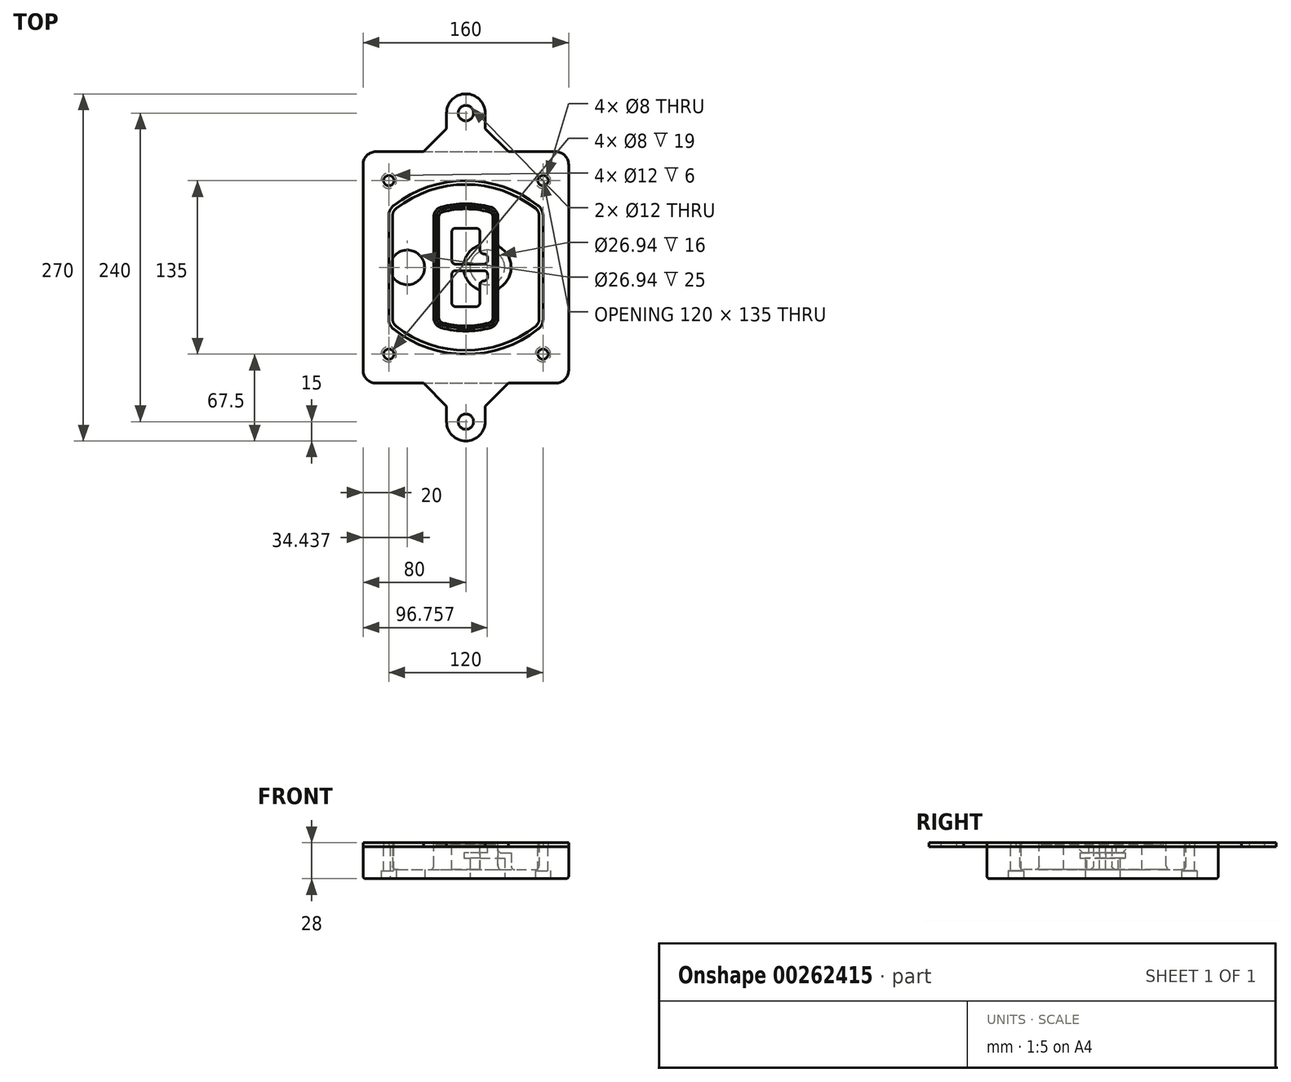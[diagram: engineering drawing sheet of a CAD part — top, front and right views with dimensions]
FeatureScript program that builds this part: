
annotation { "Feature Type Name" : "Feature", "Feature Type Description" : "" }
export const myFeature = defineFeature(function(context is Context, id is Id, definition is map)
    precondition{}
    {
        {
            var Q0;
            Q0=qCreatedBy(makeId("Top.planeOp"),FACE);
            var sketch = newSketch(context, id + "F0", { "sketchPlane" : qUnion([Q0])});
            skPoint(sketch, "E0.rect.middle", {"position": v(0, 0) * mm});
            skLineSegment(sketch, "E1.bottom", {"start": v(-70, -90) * mm, "end": v(70, -90) * mm});
            skLineSegment(sketch, "E1.top", {"start": v(-70, 90) * mm, "end": v(70, 90) * mm});
            skLineSegment(sketch, "E1.left", {"start": v(-80, -80) * mm, "end": v(-80, 80) * mm});
            skLineSegment(sketch, "E1.right", {"start": v(80, -80) * mm, "end": v(80, 80) * mm});
            skLineSegment(sketch, "E2", {"start": v(-80, 90) * mm, "end": v(80, -90) * mm, "construction": true});
            skLineSegment(sketch, "E3", {"start": v(80, 90) * mm, "end": v(-80, -90) * mm, "construction": true});
            skCircle(sketch, "E4", {"center": v(-60, 67.5) * mm, "radius": 4 * mm});
            skCircle(sketch, "E5", {"center": v(60, 67.5) * mm, "radius": 4 * mm});
            skCircle(sketch, "E6", {"center": v(60, -67.5) * mm, "radius": 4 * mm});
            skCircle(sketch, "E7", {"center": v(-60, -67.5) * mm, "radius": 4 * mm});
            skLineSegment(sketch, "E8", {"start": v(-60, 67.5) * mm, "end": v(60, 67.5) * mm, "construction": true});
            skLineSegment(sketch, "E9", {"start": v(60, 67.5) * mm, "end": v(60, -67.5) * mm, "construction": true});
            skLineSegment(sketch, "E10", {"start": v(60, -67.5) * mm, "end": v(-60, -67.5) * mm, "construction": true});
            skLineSegment(sketch, "E11", {"start": v(-60, -67.5) * mm, "end": v(-60, 67.5) * mm, "construction": true});
            skLineSegment(sketch, "E12", {"start": v(-60, 40.3) * mm, "end": v(-60, -40.3) * mm});
            skLineSegment(sketch, "E13", {"start": v(60, 40.3) * mm, "end": v(60, -40.3) * mm});
            skArc(sketch, "E14", {"start": v(56.15, 48.18) * mm, "mid": v(0, 67.5) * mm, "end": v(-56.15, 48.18) * mm});
            skArc(sketch, "E15", {"start": v(-56.15, -48.18) * mm, "mid": v(0, -67.5) * mm, "end": v(56.15, -48.18) * mm});
            skLineSegment(sketch, "E16", {"start": v(-60, 0) * mm, "end": v(60, 0) * mm, "construction": true});
            skPoint(sketch, "E17.visualSharp", {"position": v(-60, -45) * mm});
            skArc(sketch, "E17.filletArc", {"start": v(-60, -40.3) * mm, "mid": v(-58.99, -44.68) * mm, "end": v(-56.15, -48.18) * mm});
            skPoint(sketch, "E18.visualSharp", {"position": v(-60, 45) * mm});
            skArc(sketch, "E18.filletArc", {"start": v(-56.15, 48.18) * mm, "mid": v(-58.99, 44.68) * mm, "end": v(-60, 40.3) * mm});
            skPoint(sketch, "E19.visualSharp", {"position": v(60, 45) * mm});
            skArc(sketch, "E19.filletArc", {"start": v(60, 40.3) * mm, "mid": v(58.99, 44.68) * mm, "end": v(56.15, 48.18) * mm});
            skPoint(sketch, "E20.visualSharp", {"position": v(60, -45) * mm});
            skArc(sketch, "E20.filletArc", {"start": v(56.15, -48.18) * mm, "mid": v(58.99, -44.68) * mm, "end": v(60, -40.3) * mm});
            skPoint(sketch, "E21.visualSharp", {"position": v(-80, 90) * mm});
            skArc(sketch, "E21.filletArc", {"start": v(-70, 90) * mm, "mid": v(-77.07, 87.07) * mm, "end": v(-80, 80) * mm});
            skPoint(sketch, "E22.visualSharp", {"position": v(80, 90) * mm});
            skArc(sketch, "E22.filletArc", {"start": v(80, 80) * mm, "mid": v(77.07, 87.07) * mm, "end": v(70, 90) * mm});
            skPoint(sketch, "E23.visualSharp", {"position": v(80, -90) * mm});
            skArc(sketch, "E23.filletArc", {"start": v(70, -90) * mm, "mid": v(77.07, -87.07) * mm, "end": v(80, -80) * mm});
            skPoint(sketch, "E24.visualSharp", {"position": v(-80, -90) * mm});
            skArc(sketch, "E24.filletArc", {"start": v(-80, -80) * mm, "mid": v(-77.07, -87.07) * mm, "end": v(-70, -90) * mm});
            skArc(sketch, "E25.0", {"start": v(57, 40.3) * mm, "mid": v(56.3, 43.36) * mm, "end": v(54.3, 45.81) * mm});
            skLineSegment(sketch, "E25.1", {"start": v(57, 40.3) * mm, "end": v(57, -40.3) * mm});
            skArc(sketch, "E25.2", {"start": v(54.3, -45.81) * mm, "mid": v(56.3, -43.36) * mm, "end": v(57, -40.3) * mm});
            skArc(sketch, "E25.3", {"start": v(-54.3, -45.81) * mm, "mid": v(0, -64.5) * mm, "end": v(54.3, -45.81) * mm});
            skArc(sketch, "E25.4", {"start": v(-57, -40.3) * mm, "mid": v(-56.3, -43.36) * mm, "end": v(-54.3, -45.81) * mm});
            skArc(sketch, "E25.5", {"start": v(54.3, 45.81) * mm, "mid": v(0, 64.5) * mm, "end": v(-54.3, 45.81) * mm});
            skLineSegment(sketch, "E25.6", {"start": v(-57, 40.3) * mm, "end": v(-57, -40.3) * mm});
            skArc(sketch, "E25.7", {"start": v(-54.3, 45.81) * mm, "mid": v(-56.3, 43.36) * mm, "end": v(-57, 40.3) * mm});
            skArc(sketch, "E26.0", {"start": v(-58.62, 51.33) * mm, "mid": v(-62.58, 46.43) * mm, "end": v(-64, 40.3) * mm});
            skArc(sketch, "E26.1", {"start": v(58.62, 51.33) * mm, "mid": v(0, 71.5) * mm, "end": v(-58.62, 51.33) * mm});
            skArc(sketch, "E26.2", {"start": v(64, 40.3) * mm, "mid": v(62.58, 46.43) * mm, "end": v(58.62, 51.33) * mm});
            skLineSegment(sketch, "E26.3", {"start": v(64, 40.3) * mm, "end": v(64, -40.3) * mm});
            skArc(sketch, "E26.4", {"start": v(58.62, -51.33) * mm, "mid": v(62.58, -46.43) * mm, "end": v(64, -40.3) * mm});
            skLineSegment(sketch, "E26.5", {"start": v(-64, 40.3) * mm, "end": v(-64, -40.3) * mm});
            skArc(sketch, "E26.6", {"start": v(-58.62, -51.33) * mm, "mid": v(0, -71.5) * mm, "end": v(58.62, -51.33) * mm});
            skArc(sketch, "E26.7", {"start": v(-64, -40.3) * mm, "mid": v(-62.58, -46.43) * mm, "end": v(-58.62, -51.33) * mm});
            skSolve(sketch);
        }
        {
            var Q0;
            Q0=makeQuery(id+"F0.imprint","IMPRINT",FACE,{"disambiguationData":[TD([[makeQuery(id+"F0.imprint","IMPRINT",EDGE,{"derivedFrom":sQuery(id+"F0.wireOp",EDGE,"E1.bottom")}),1.0]])]});
            var Q1;
            Q1=makeQuery(id+"F0.imprint","IMPRINT",FACE,{"disambiguationData":[TD([[makeQuery(id+"F0.imprint","IMPRINT",EDGE,{"derivedFrom":sQuery(id+"F0.wireOp",EDGE,"E12")}),1.0]])]});
            var Q2;
            Q2=makeQuery(id+"F0.imprint","IMPRINT",FACE,{"disambiguationData":[TD([[makeQuery(id+"F0.imprint","IMPRINT",EDGE,{"derivedFrom":sQuery(id+"F0.wireOp",EDGE,"E25.0")}),1.0]])]});
            var Q3;
            Q3=makeQuery(id+"F0.imprint","IMPRINT",FACE,{"disambiguationData":[TD([[makeQuery(id+"F0.imprint","IMPRINT",EDGE,{"derivedFrom":sQuery(id+"F0.wireOp",EDGE,"E12")}),-1.0]])]});
            extrude(context, id + "F1", {"entities" : qUnion([Q0, Q1, Q2, Q3]), "oppositeDirection" : true, "depth" : 25 * mm});
        }
        {
            var Q0;
            Q0=makeQuery(id+"F0.imprint","IMPRINT",FACE,{"disambiguationData":[TD([[makeQuery(id+"F0.imprint","IMPRINT",EDGE,{"derivedFrom":sQuery(id+"F0.wireOp",EDGE,"E12")}),1.0]])]});
            extrude(context, id + "F2", {"entities" : qUnion([Q0]), "operationType" : NewBodyOperationType.ADD, "depth" : 3 * mm});
        }
        {
            var Q0;
            Q0=makeQuery(id+"F0.imprint","IMPRINT",FACE,{"disambiguationData":[TD([[makeQuery(id+"F0.imprint","IMPRINT",EDGE,{"derivedFrom":sQuery(id+"F0.wireOp",EDGE,"E25.0")}),1.0]])]});
            extrude(context, id + "F3", {"entities" : qUnion([Q0]), "operationType" : NewBodyOperationType.REMOVE, "oppositeDirection" : true, "depth" : 18 * mm});
        }
        {
            var Q0;
            Q0=makeQuery(id+"F2.opExtrude","CAP_FACE",FACE,{"disambiguationData":[OSD([sQuery(id+"F0.wireOp",EDGE,"E12"),sQuery(id+"F0.wireOp",EDGE,"E13"),sQuery(id+"F0.wireOp",EDGE,"E14"),sQuery(id+"F0.wireOp",EDGE,"E15"),sQuery(id+"F0.wireOp",EDGE,"E17.filletArc"),sQuery(id+"F0.wireOp",EDGE,"E18.filletArc"),sQuery(id+"F0.wireOp",EDGE,"E19.filletArc"),sQuery(id+"F0.wireOp",EDGE,"E20.filletArc"),sQuery(id+"F0.wireOp",EDGE,"E25.0"),sQuery(id+"F0.wireOp",EDGE,"E25.1"),sQuery(id+"F0.wireOp",EDGE,"E25.2"),sQuery(id+"F0.wireOp",EDGE,"E25.3"),sQuery(id+"F0.wireOp",EDGE,"E25.4"),sQuery(id+"F0.wireOp",EDGE,"E25.5"),sQuery(id+"F0.wireOp",EDGE,"E25.6"),sQuery(id+"F0.wireOp",EDGE,"E25.7")])],"isStart":false});
            var sketch = newSketch(context, id + "F4", { "sketchPlane" : qUnion([Q0])});
            skArc(sketch, "E27.0", {"start": v(-19.08, -46.97) * mm, "mid": v(0, -49.5) * mm, "end": v(19.08, -46.97) * mm});
            skArc(sketch, "E28.0", {"start": v(19.08, 46.97) * mm, "mid": v(0, 49.5) * mm, "end": v(-19.08, 46.97) * mm});
            skLineSegment(sketch, "E29", {"start": v(-25, 39.25) * mm, "end": v(-25, -39.25) * mm});
            skLineSegment(sketch, "E30", {"start": v(25, 39.25) * mm, "end": v(25, -39.25) * mm});
            skLineSegment(sketch, "E31", {"start": v(-25, 45.1) * mm, "end": v(25, 45.1) * mm, "construction": true});
            skLineSegment(sketch, "E32", {"start": v(-25, -45.1) * mm, "end": v(25, -45.1) * mm, "construction": true});
            skPoint(sketch, "E33.visualSharp", {"position": v(-25, 45.1) * mm});
            skArc(sketch, "E33.filletArc", {"start": v(-19.08, 46.97) * mm, "mid": v(-23.35, 44.11) * mm, "end": v(-25, 39.25) * mm});
            skPoint(sketch, "E34.visualSharp", {"position": v(25, 45.1) * mm});
            skArc(sketch, "E34.filletArc", {"start": v(25, 39.25) * mm, "mid": v(23.35, 44.11) * mm, "end": v(19.08, 46.97) * mm});
            skPoint(sketch, "E35.visualSharp", {"position": v(25, -45.1) * mm});
            skArc(sketch, "E35.filletArc", {"start": v(19.08, -46.97) * mm, "mid": v(23.35, -44.11) * mm, "end": v(25, -39.25) * mm});
            skPoint(sketch, "E36.visualSharp", {"position": v(-25, -45.1) * mm});
            skArc(sketch, "E36.filletArc", {"start": v(-25, -39.25) * mm, "mid": v(-23.35, -44.11) * mm, "end": v(-19.08, -46.97) * mm});
            skArc(sketch, "E37.0", {"start": v(54.3, 45.81) * mm, "mid": v(0, 64.5) * mm, "end": v(-54.3, 45.81) * mm});
            skArc(sketch, "E37.1", {"start": v(-54.3, 45.81) * mm, "mid": v(-56.3, 43.36) * mm, "end": v(-57, 40.3) * mm});
            skLineSegment(sketch, "E37.2", {"start": v(-57, 40.3) * mm, "end": v(-57, -40.3) * mm});
            skArc(sketch, "E37.3", {"start": v(-57, -40.3) * mm, "mid": v(-56.3, -43.36) * mm, "end": v(-54.3, -45.81) * mm});
            skArc(sketch, "E37.4", {"start": v(-54.3, -45.81) * mm, "mid": v(0, -64.5) * mm, "end": v(54.3, -45.81) * mm});
            skArc(sketch, "E37.5", {"start": v(54.3, -45.81) * mm, "mid": v(56.3, -43.36) * mm, "end": v(57, -40.3) * mm});
            skLineSegment(sketch, "E37.6", {"start": v(57, 40.3) * mm, "end": v(57, -40.3) * mm});
            skArc(sketch, "E37.7", {"start": v(57, 40.3) * mm, "mid": v(56.3, 43.36) * mm, "end": v(54.3, 45.81) * mm});
            skLineSegment(sketch, "E38.0", {"start": v(23, 39.25) * mm, "end": v(23, -39.25) * mm});
            skArc(sketch, "E38.1", {"start": v(18.56, -45.04) * mm, "mid": v(21.76, -42.9) * mm, "end": v(23, -39.25) * mm});
            skArc(sketch, "E38.2", {"start": v(-18.56, -45.04) * mm, "mid": v(0, -47.5) * mm, "end": v(18.56, -45.04) * mm});
            skArc(sketch, "E38.3", {"start": v(-23, -39.25) * mm, "mid": v(-21.76, -42.9) * mm, "end": v(-18.56, -45.04) * mm});
            skLineSegment(sketch, "E38.4", {"start": v(-23, 39.25) * mm, "end": v(-23, -39.25) * mm});
            skArc(sketch, "E38.5", {"start": v(23, 39.25) * mm, "mid": v(21.76, 42.9) * mm, "end": v(18.56, 45.04) * mm});
            skArc(sketch, "E38.6", {"start": v(-18.56, 45.04) * mm, "mid": v(-21.76, 42.9) * mm, "end": v(-23, 39.25) * mm});
            skArc(sketch, "E38.7", {"start": v(18.56, 45.04) * mm, "mid": v(0, 47.5) * mm, "end": v(-18.56, 45.04) * mm});
            skArc(sketch, "E39.0", {"start": v(21, 39.25) * mm, "mid": v(20.18, 41.68) * mm, "end": v(18.04, 43.1) * mm});
            skLineSegment(sketch, "E39.1", {"start": v(21, 39.25) * mm, "end": v(21, -39.25) * mm});
            skArc(sketch, "E39.2", {"start": v(18.04, -43.1) * mm, "mid": v(20.18, -41.68) * mm, "end": v(21, -39.25) * mm});
            skArc(sketch, "E39.3", {"start": v(-18.04, -43.1) * mm, "mid": v(0, -45.5) * mm, "end": v(18.04, -43.1) * mm});
            skArc(sketch, "E39.4", {"start": v(-21, -39.25) * mm, "mid": v(-20.18, -41.68) * mm, "end": v(-18.04, -43.1) * mm});
            skArc(sketch, "E39.5", {"start": v(18.04, 43.1) * mm, "mid": v(0, 45.5) * mm, "end": v(-18.04, 43.1) * mm});
            skLineSegment(sketch, "E39.6", {"start": v(-21, 39.25) * mm, "end": v(-21, -39.25) * mm});
            skArc(sketch, "E39.7", {"start": v(-18.04, 43.1) * mm, "mid": v(-20.18, 41.68) * mm, "end": v(-21, 39.25) * mm});
            skLineSegment(sketch, "E40", {"start": v(-25, 0) * mm, "end": v(25, 0) * mm, "construction": true});
            skLineSegment(sketch, "E41", {"start": v(-11, 5.5) * mm, "end": v(-11, 27.5) * mm});
            skLineSegment(sketch, "E42", {"start": v(-8, 30.5) * mm, "end": v(8, 30.5) * mm});
            skLineSegment(sketch, "E43", {"start": v(11, 27.5) * mm, "end": v(11, 13.5) * mm});
            skLineSegment(sketch, "E44", {"start": v(14, 10.5) * mm, "end": v(14, 10.5) * mm});
            skLineSegment(sketch, "E45", {"start": v(17, 7.5) * mm, "end": v(17, 5.5) * mm});
            skLineSegment(sketch, "E46", {"start": v(14, 2.5) * mm, "end": v(-8, 2.5) * mm});
            skPoint(sketch, "E47.visualSharp", {"position": v(-11, 30.5) * mm});
            skArc(sketch, "E47.filletArc", {"start": v(-8, 30.5) * mm, "mid": v(-10.12, 29.62) * mm, "end": v(-11, 27.5) * mm});
            skPoint(sketch, "E48.visualSharp", {"position": v(11, 30.5) * mm});
            skArc(sketch, "E48.filletArc", {"start": v(11, 27.5) * mm, "mid": v(10.12, 29.62) * mm, "end": v(8, 30.5) * mm});
            skPoint(sketch, "E49.visualSharp", {"position": v(11, 10.5) * mm});
            skArc(sketch, "E49.filletArc", {"start": v(11, 13.5) * mm, "mid": v(11.88, 11.38) * mm, "end": v(14, 10.5) * mm});
            skPoint(sketch, "E50.visualSharp", {"position": v(17, 10.5) * mm});
            skArc(sketch, "E50.filletArc", {"start": v(17, 7.5) * mm, "mid": v(16.12, 9.62) * mm, "end": v(14, 10.5) * mm});
            skPoint(sketch, "E51.visualSharp", {"position": v(17, 2.5) * mm});
            skArc(sketch, "E51.filletArc", {"start": v(14, 2.5) * mm, "mid": v(16.12, 3.38) * mm, "end": v(17, 5.5) * mm});
            skPoint(sketch, "E52.visualSharp", {"position": v(-11, 2.5) * mm});
            skArc(sketch, "E52.filletArc", {"start": v(-11, 5.5) * mm, "mid": v(-10.12, 3.38) * mm, "end": v(-8, 2.5) * mm});
            skLineSegment(sketch, "E53.0.MirrorCS", {"start": v(14, -2.5) * mm, "end": v(-8, -2.5) * mm});
            skArc(sketch, "E54.0.MirrorCS", {"start": v(-11, -5.5) * mm, "mid": v(-10.12, -3.38) * mm, "end": v(-8, -2.5) * mm});
            skLineSegment(sketch, "E55.0.MirrorCS", {"start": v(-11, -5.5) * mm, "end": v(-11, -27.5) * mm});
            skArc(sketch, "E56.0.MirrorCS", {"start": v(-8, -30.5) * mm, "mid": v(-10.12, -29.62) * mm, "end": v(-11, -27.5) * mm});
            skLineSegment(sketch, "E57.0.MirrorCS", {"start": v(-8, -30.5) * mm, "end": v(8, -30.5) * mm});
            skArc(sketch, "E58.0.MirrorCS", {"start": v(11, -27.5) * mm, "mid": v(10.12, -29.62) * mm, "end": v(8, -30.5) * mm});
            skLineSegment(sketch, "E59.0.MirrorCS", {"start": v(11, -27.5) * mm, "end": v(11, -13.5) * mm});
            skArc(sketch, "E60.0.MirrorCS", {"start": v(11, -13.5) * mm, "mid": v(11.88, -11.38) * mm, "end": v(14, -10.5) * mm});
            skArc(sketch, "E61.0.MirrorCS", {"start": v(17, -7.5) * mm, "mid": v(16.12, -9.62) * mm, "end": v(14, -10.5) * mm});
            skLineSegment(sketch, "E62.0.MirrorCS", {"start": v(17, -7.5) * mm, "end": v(17, -5.5) * mm});
            skArc(sketch, "E63.0.MirrorCS", {"start": v(14, -2.5) * mm, "mid": v(16.12, -3.38) * mm, "end": v(17, -5.5) * mm});
            skSolve(sketch);
        }
        {
            var Q0;
            Q0=makeQuery(id+"F4.imprint","IMPRINT",FACE,{"disambiguationData":[TD([[makeQuery(id+"F4.imprint","IMPRINT",EDGE,{"derivedFrom":sQuery(id+"F4.wireOp",EDGE,"E27.0")}),1.0]])]});
            var Q1;
            Q1=makeQuery(id+"F4.imprint","IMPRINT",FACE,{"disambiguationData":[TD([[makeQuery(id+"F4.imprint","IMPRINT",EDGE,{"derivedFrom":sQuery(id+"F4.wireOp",EDGE,"E38.0")}),-1.0]])]});
            var Q2;
            Q2=makeQuery(id+"F4.imprint","IMPRINT",FACE,{"disambiguationData":[TD([[makeQuery(id+"F4.imprint","IMPRINT",EDGE,{"derivedFrom":sQuery(id+"F4.wireOp",EDGE,"E39.0")}),1.0]])]});
            extrude(context, id + "F5", {"entities" : qUnion([Q0, Q1, Q2]), "operationType" : NewBodyOperationType.ADD, "endBound" : BoundingType.UP_TO_NEXT, "oppositeDirection" : true, "depth" : 25 * mm});
        }
        {
            var Q0;
            Q0=makeQuery(id+"F4.imprint","IMPRINT",FACE,{"disambiguationData":[TD([[makeQuery(id+"F4.imprint","IMPRINT",EDGE,{"derivedFrom":sQuery(id+"F4.wireOp",EDGE,"E38.0")}),-1.0]])]});
            extrude(context, id + "F6", {"entities" : qUnion([Q0]), "operationType" : NewBodyOperationType.REMOVE, "oppositeDirection" : true, "depth" : 2 * mm});
        }
        {
            var Q0;
            Q0=makeQuery(id+"F1.opExtrude","CAP_FACE",FACE,{"disambiguationData":[OSD([sQuery(id+"F0.wireOp",EDGE,"E1.bottom"),sQuery(id+"F0.wireOp",EDGE,"E1.top"),sQuery(id+"F0.wireOp",EDGE,"E1.left"),sQuery(id+"F0.wireOp",EDGE,"E1.right"),sQuery(id+"F0.wireOp",EDGE,"E4"),sQuery(id+"F0.wireOp",EDGE,"E5"),sQuery(id+"F0.wireOp",EDGE,"E6"),sQuery(id+"F0.wireOp",EDGE,"E7"),sQuery(id+"F0.wireOp",EDGE,"E21.filletArc"),sQuery(id+"F0.wireOp",EDGE,"E22.filletArc"),sQuery(id+"F0.wireOp",EDGE,"E23.filletArc"),sQuery(id+"F0.wireOp",EDGE,"E24.filletArc")])],"isStart":false});
            var sketch = newSketch(context, id + "F7", { "sketchPlane" : qUnion([Q0])});
            skCircle(sketch, "E64", {"center": v(16.76, 0) * mm, "radius": 13.47 * mm});
            skCircle(sketch, "E65", {"center": v(-45.56, 0) * mm, "radius": 13.47 * mm});
            skLineSegment(sketch, "E66", {"start": v(80, 0) * mm, "end": v(-80, 0) * mm});
            skCircle(sketch, "E67", {"center": v(16.76, 0) * mm, "radius": 18.47 * mm});
            skCircle(sketch, "E68", {"center": v(60, -67.5) * mm, "radius": 6 * mm});
            skCircle(sketch, "E69", {"center": v(-60, -67.5) * mm, "radius": 6 * mm});
            skCircle(sketch, "E70", {"center": v(-60, 67.5) * mm, "radius": 6 * mm});
            skCircle(sketch, "E71", {"center": v(60, 67.5) * mm, "radius": 6 * mm});
            skSolve(sketch);
        }
        {
            var Q0;
            {var subQ1=sQuery(id+"F7.wireOp",EDGE,"E66");var subQ4=sQuery(id+"F7.wireOp",EDGE,"E64");var subQ6=makeQuery(id+"F7.imprint","INTERSECT",VERTEX,{"disambiguationData":[OD(0.0)],"derivedFrom":[subQ4,subQ1]});Q0=makeQuery(id+"F7.imprint","IMPRINT",FACE,{"disambiguationData":[TD([[makeQuery(id+"F7.imprint","IMPRINT",EDGE,{"disambiguationData":[TD([[subQ6,-1.0]])],"derivedFrom":subQ4}),-1.0]])]});}
            var Q1;
            {var subQ0=sQuery(id+"F7.wireOp",EDGE,"E66");var subQ1=sQuery(id+"F7.wireOp",EDGE,"E64");var subQ3=makeQuery(id+"F7.imprint","INTERSECT",VERTEX,{"disambiguationData":[OD(0.0)],"derivedFrom":[subQ1,subQ0]});Q1=makeQuery(id+"F7.imprint","IMPRINT",FACE,{"disambiguationData":[TD([[makeQuery(id+"F7.imprint","IMPRINT",EDGE,{"disambiguationData":[TD([[subQ3,-1.0]])],"derivedFrom":subQ1}),1.0]])]});}
            var Q2;
            {var subQ0=sQuery(id+"F7.wireOp",EDGE,"E66");var subQ1=sQuery(id+"F7.wireOp",EDGE,"E64");var subQ3=makeQuery(id+"F7.imprint","INTERSECT",VERTEX,{"disambiguationData":[OD(0.0)],"derivedFrom":[subQ1,subQ0]});Q2=makeQuery(id+"F7.imprint","IMPRINT",FACE,{"disambiguationData":[TD([[makeQuery(id+"F7.imprint","IMPRINT",EDGE,{"disambiguationData":[TD([[subQ3,1.0]])],"derivedFrom":subQ1}),1.0]])]});}
            var Q3;
            {var subQ1=sQuery(id+"F7.wireOp",EDGE,"E66");var subQ4=sQuery(id+"F7.wireOp",EDGE,"E64");var subQ6=makeQuery(id+"F7.imprint","INTERSECT",VERTEX,{"disambiguationData":[OD(0.0)],"derivedFrom":[subQ4,subQ1]});Q3=makeQuery(id+"F7.imprint","IMPRINT",FACE,{"disambiguationData":[TD([[makeQuery(id+"F7.imprint","IMPRINT",EDGE,{"disambiguationData":[TD([[subQ6,1.0]])],"derivedFrom":subQ4}),-1.0]])]});}
            extrude(context, id + "F8", {"entities" : qUnion([Q0, Q1, Q2, Q3]), "operationType" : NewBodyOperationType.ADD, "oppositeDirection" : true, "depth" : 20 * mm});
        }
        {
            var Q0;
            {var subQ0=sQuery(id+"F7.wireOp",EDGE,"E66");var subQ1=sQuery(id+"F7.wireOp",EDGE,"E64");var subQ3=makeQuery(id+"F7.imprint","INTERSECT",VERTEX,{"disambiguationData":[OD(0.0)],"derivedFrom":[subQ1,subQ0]});Q0=makeQuery(id+"F7.imprint","IMPRINT",FACE,{"disambiguationData":[TD([[makeQuery(id+"F7.imprint","IMPRINT",EDGE,{"disambiguationData":[TD([[subQ3,-1.0]])],"derivedFrom":subQ1}),1.0]])]});}
            var Q1;
            {var subQ0=sQuery(id+"F7.wireOp",EDGE,"E66");var subQ1=sQuery(id+"F7.wireOp",EDGE,"E64");var subQ3=makeQuery(id+"F7.imprint","INTERSECT",VERTEX,{"disambiguationData":[OD(0.0)],"derivedFrom":[subQ1,subQ0]});Q1=makeQuery(id+"F7.imprint","IMPRINT",FACE,{"disambiguationData":[TD([[makeQuery(id+"F7.imprint","IMPRINT",EDGE,{"disambiguationData":[TD([[subQ3,1.0]])],"derivedFrom":subQ1}),1.0]])]});}
            extrude(context, id + "F9", {"entities" : qUnion([Q0, Q1]), "operationType" : NewBodyOperationType.REMOVE, "oppositeDirection" : true, "depth" : 16 * mm});
        }
        {
            var Q0;
            {var subQ0=sQuery(id+"F7.wireOp",EDGE,"E66");var subQ1=sQuery(id+"F7.wireOp",EDGE,"E65");var subQ3=makeQuery(id+"F7.imprint","INTERSECT",VERTEX,{"disambiguationData":[OD(0.0)],"derivedFrom":[subQ1,subQ0]});Q0=makeQuery(id+"F7.imprint","IMPRINT",FACE,{"disambiguationData":[TD([[makeQuery(id+"F7.imprint","IMPRINT",EDGE,{"disambiguationData":[TD([[subQ3,-1.0]])],"derivedFrom":subQ1}),1.0]])]});}
            var Q1;
            {var subQ0=sQuery(id+"F7.wireOp",EDGE,"E66");var subQ1=sQuery(id+"F7.wireOp",EDGE,"E65");var subQ3=makeQuery(id+"F7.imprint","INTERSECT",VERTEX,{"disambiguationData":[OD(0.0)],"derivedFrom":[subQ1,subQ0]});Q1=makeQuery(id+"F7.imprint","IMPRINT",FACE,{"disambiguationData":[TD([[makeQuery(id+"F7.imprint","IMPRINT",EDGE,{"disambiguationData":[TD([[subQ3,1.0]])],"derivedFrom":subQ1}),1.0]])]});}
            extrude(context, id + "F10", {"entities" : qUnion([Q0, Q1]), "operationType" : NewBodyOperationType.REMOVE, "oppositeDirection" : true, "depth" : 25 * mm});
        }
        {
            var Q0;
            Q0=makeQuery(id+"F7.imprint","IMPRINT",FACE,{"disambiguationData":[TD([[makeQuery(id+"F7.imprint","IMPRINT",EDGE,{"derivedFrom":sQuery(id+"F7.wireOp",EDGE,"E68")}),1.0]])]});
            var Q1;
            Q1=makeQuery(id+"F7.imprint","IMPRINT",FACE,{"disambiguationData":[TD([[makeQuery(id+"F7.imprint","IMPRINT",EDGE,{"derivedFrom":makeQuery(id+"F1.opExtrude","CAP_EDGE",EDGE,{"disambiguationData":[OSD([sQuery(id+"F0.wireOp",EDGE,"E5")])],"isStart":false})}),-1.0]])]});
            var Q2;
            Q2=makeQuery(id+"F7.imprint","IMPRINT",FACE,{"disambiguationData":[TD([[makeQuery(id+"F7.imprint","IMPRINT",EDGE,{"derivedFrom":sQuery(id+"F7.wireOp",EDGE,"E69")}),1.0]])]});
            var Q3;
            Q3=makeQuery(id+"F7.imprint","IMPRINT",FACE,{"disambiguationData":[TD([[makeQuery(id+"F7.imprint","IMPRINT",EDGE,{"derivedFrom":makeQuery(id+"F1.opExtrude","CAP_EDGE",EDGE,{"disambiguationData":[OSD([sQuery(id+"F0.wireOp",EDGE,"E4")])],"isStart":false})}),-1.0]])]});
            var Q4;
            Q4=makeQuery(id+"F7.imprint","IMPRINT",FACE,{"disambiguationData":[TD([[makeQuery(id+"F7.imprint","IMPRINT",EDGE,{"derivedFrom":sQuery(id+"F7.wireOp",EDGE,"E70")}),1.0]])]});
            var Q5;
            Q5=makeQuery(id+"F7.imprint","IMPRINT",FACE,{"disambiguationData":[TD([[makeQuery(id+"F7.imprint","IMPRINT",EDGE,{"derivedFrom":makeQuery(id+"F1.opExtrude","CAP_EDGE",EDGE,{"disambiguationData":[OSD([sQuery(id+"F0.wireOp",EDGE,"E7")])],"isStart":false})}),-1.0]])]});
            var Q6;
            Q6=makeQuery(id+"F7.imprint","IMPRINT",FACE,{"disambiguationData":[TD([[makeQuery(id+"F7.imprint","IMPRINT",EDGE,{"derivedFrom":sQuery(id+"F7.wireOp",EDGE,"E71")}),1.0]])]});
            var Q7;
            Q7=makeQuery(id+"F7.imprint","IMPRINT",FACE,{"disambiguationData":[TD([[makeQuery(id+"F7.imprint","IMPRINT",EDGE,{"derivedFrom":makeQuery(id+"F1.opExtrude","CAP_EDGE",EDGE,{"disambiguationData":[OSD([sQuery(id+"F0.wireOp",EDGE,"E6")])],"isStart":false})}),-1.0]])]});
            extrude(context, id + "F11", {"entities" : qUnion([Q0, Q1, Q2, Q3, Q4, Q5, Q6, Q7]), "operationType" : NewBodyOperationType.REMOVE, "oppositeDirection" : true, "depth" : 6 * mm});
        }
        {
            var Q0;
            Q0=makeQuery(id+"F9.boolean.opBoolean","COPY",FACE,{"derivedFrom":makeQuery(id+"F9.opExtrude","CAP_FACE",FACE,{"disambiguationData":[OSD([sQuery(id+"F7.wireOp",EDGE,"E64")])],"isStart":false})});
            var sketch = newSketch(context, id + "F12", { "sketchPlane" : qUnion([Q0])});
            skArc(sketch, "E72.0", {"start": v(11, 17.55) * mm, "mid": v(2.57, 11.82) * mm, "end": v(-1.54, 2.5) * mm});
            skArc(sketch, "E72.1", {"start": v(-1.54, -2.5) * mm, "mid": v(2.57, -11.82) * mm, "end": v(11, -17.55) * mm});
            skLineSegment(sketch, "E73", {"start": v(-1.54, -2.5) * mm, "end": v(14, -2.5) * mm});
            skLineSegment(sketch, "E74.0", {"start": v(14, 2.5) * mm, "end": v(-1.54, 2.5) * mm});
            skArc(sketch, "E74.1", {"start": v(14, 2.5) * mm, "mid": v(16.12, 3.38) * mm, "end": v(17, 5.5) * mm});
            skLineSegment(sketch, "E74.2", {"start": v(17, 7.5) * mm, "end": v(17, 5.5) * mm});
            skArc(sketch, "E74.3", {"start": v(17, 7.5) * mm, "mid": v(16.12, 9.62) * mm, "end": v(14, 10.5) * mm});
            skArc(sketch, "E74.4", {"start": v(11, 13.5) * mm, "mid": v(11.88, 11.38) * mm, "end": v(14, 10.5) * mm});
            skLineSegment(sketch, "E74.5", {"start": v(11, 17.55) * mm, "end": v(11, 13.5) * mm});
            skLineSegment(sketch, "E74.7", {"start": v(14, -2.5) * mm, "end": v(-1.54, -2.5) * mm});
            skArc(sketch, "E74.8", {"start": v(14, -2.5) * mm, "mid": v(16.12, -3.38) * mm, "end": v(17, -5.5) * mm});
            skLineSegment(sketch, "E74.9", {"start": v(17, -7.5) * mm, "end": v(17, -5.5) * mm});
            skArc(sketch, "E74.10", {"start": v(17, -7.5) * mm, "mid": v(16.12, -9.62) * mm, "end": v(14, -10.5) * mm});
            skArc(sketch, "E74.11", {"start": v(11, -13.5) * mm, "mid": v(11.88, -11.38) * mm, "end": v(14, -10.5) * mm});
            skLineSegment(sketch, "E74.12", {"start": v(11, -17.55) * mm, "end": v(11, -13.5) * mm});
            skPoint(sketch, "E75.orphan", {"position": v(11, -27.5) * mm});
            skPoint(sketch, "E76.orphan", {"position": v(-8, -2.5) * mm});
            skPoint(sketch, "E77.orphan", {"position": v(-8, 2.5) * mm});
            skPoint(sketch, "E78.orphan", {"position": v(11, 27.5) * mm});
            skSolve(sketch);
        }
        {
            var Q0;
            {var subQ7=sQuery(id+"F12.wireOp",EDGE,"E72.0");var subQ14=sQuery(id+"F12.wireOp",EDGE,"E72.1");var subQ16=sQuery(id+"F12.wireOp",EDGE,"E74.1");var subQ18=sQuery(id+"F12.wireOp",EDGE,"E74.8");Q0=qUnion([makeQuery(id+"F12.imprint","IMPRINT",FACE,{"disambiguationData":[TD([[makeQuery(id+"F12.imprint","IMPRINT",EDGE,{"derivedFrom":subQ7}),1.0]])]}),makeQuery(id+"F12.imprint","IMPRINT",FACE,{"disambiguationData":[TD([[makeQuery(id+"F12.imprint","IMPRINT",EDGE,{"derivedFrom":subQ14}),1.0]])]}),makeQuery(id+"F12.imprint","IMPRINT",FACE,{"disambiguationData":[TD([[makeQuery(id+"F12.imprint","IMPRINT",EDGE,{"derivedFrom":subQ16}),1.0]])]}),makeQuery(id+"F12.imprint","IMPRINT",FACE,{"disambiguationData":[TD([[makeQuery(id+"F12.imprint","IMPRINT",EDGE,{"derivedFrom":subQ18}),-1.0]])]})]);}
            var Q1;
            Q1=makeQuery(id+"F5.boolean.opBoolean","SPLIT",FACE,{"disambiguationData":[TD([makeQuery(id+"F5.opExtrude","SWEPT_FACE",FACE,{"disambiguationData":[OSD([sQuery(id+"F4.wireOp",EDGE,"E41")])]})])],"derivedFrom":makeQuery(id+"F3.boolean.opBoolean","COPY",FACE,{"derivedFrom":makeQuery(id+"F3.opExtrude","CAP_FACE",FACE,{"disambiguationData":[OSD([sQuery(id+"F0.wireOp",EDGE,"E25.0"),sQuery(id+"F0.wireOp",EDGE,"E25.1"),sQuery(id+"F0.wireOp",EDGE,"E25.2"),sQuery(id+"F0.wireOp",EDGE,"E25.3"),sQuery(id+"F0.wireOp",EDGE,"E25.4"),sQuery(id+"F0.wireOp",EDGE,"E25.5"),sQuery(id+"F0.wireOp",EDGE,"E25.6"),sQuery(id+"F0.wireOp",EDGE,"E25.7")])],"isStart":false})})});
            extrude(context, id + "F13", {"entities" : qUnion([Q0]), "operationType" : NewBodyOperationType.REMOVE, "endBound" : BoundingType.UP_TO_SURFACE, "endBoundEntityFace" : qUnion([Q1]), "depth" : 25 * mm});
        }
        {
            var Q0;
            Q0=makeQuery(id+"F3.boolean.opBoolean","COPY",EDGE,{"derivedFrom":makeQuery(id+"F3.opExtrude","CAP_EDGE",EDGE,{"disambiguationData":[OSD([sQuery(id+"F0.wireOp",EDGE,"E25.6")])],"isStart":false})});
            var Q1;
            Q1=makeQuery(id+"F8.boolean.opBoolean","INTERSECT",EDGE,{"derivedFrom":[makeQuery(id+"F5.opExtrude","SWEPT_FACE",FACE,{"disambiguationData":[OSD([sQuery(id+"F4.wireOp",EDGE,"E30")])]}),makeQuery(id+"F8.opExtrude","CAP_FACE",FACE,{"disambiguationData":[OSD([sQuery(id+"F7.wireOp",EDGE,"E67")])],"isStart":false})]});
            var Q2;
            Q2=makeQuery(id+"F8.boolean.opBoolean","INTERSECT",EDGE,{"disambiguationData":[OD(1.0)],"derivedFrom":[makeQuery(id+"F5.opExtrude","SWEPT_FACE",FACE,{"disambiguationData":[OSD([sQuery(id+"F4.wireOp",EDGE,"E30")])]}),makeQuery(id+"F8.opExtrude","SWEPT_FACE",FACE,{"disambiguationData":[OSD([sQuery(id+"F7.wireOp",EDGE,"E67")])]})]});
            var Q3;
            {var subQ0=sQuery(id+"F4.wireOp",EDGE,"E30");Q3=makeQuery(id+"F8.boolean.opBoolean","SPLIT",EDGE,{"disambiguationData":[TD([makeQuery(id+"F5.opExtrude","SWEPT_FACE",FACE,{"disambiguationData":[OSD([sQuery(id+"F4.wireOp",EDGE,"E35.filletArc")])]})])],"derivedFrom":makeQuery(id+"F5.opExtrude","CAP_EDGE",EDGE,{"disambiguationData":[OSD([subQ0])],"isStart":false})});}
            var Q4;
            {var subQ0=sQuery(id+"F0.wireOp",EDGE,"E25.7");var subQ1=sQuery(id+"F0.wireOp",EDGE,"E25.1");var subQ2=sQuery(id+"F0.wireOp",EDGE,"E25.6");var subQ3=sQuery(id+"F0.wireOp",EDGE,"E25.5");var subQ4=sQuery(id+"F0.wireOp",EDGE,"E25.4");var subQ5=sQuery(id+"F0.wireOp",EDGE,"E25.0");var subQ6=sQuery(id+"F0.wireOp",EDGE,"E25.2");var subQ7=sQuery(id+"F0.wireOp",EDGE,"E25.3");Q4=makeQuery(id+"F8.boolean.opBoolean","INTERSECT",EDGE,{"derivedFrom":[makeQuery(id+"F5.boolean.opBoolean","SPLIT",FACE,{"disambiguationData":[TD([makeQuery(id+"F2.opExtrude","SWEPT_FACE",FACE,{"disambiguationData":[OSD([subQ5])]})])],"derivedFrom":makeQuery(id+"F3.boolean.opBoolean","COPY",FACE,{"derivedFrom":makeQuery(id+"F3.opExtrude","CAP_FACE",FACE,{"disambiguationData":[OSD([subQ5,subQ1,subQ6,subQ7,subQ4,subQ3,subQ2,subQ0])],"isStart":false})})}),makeQuery(id+"F8.opExtrude","SWEPT_FACE",FACE,{"disambiguationData":[OSD([sQuery(id+"F7.wireOp",EDGE,"E67")])]})]});}
            var Q5;
            Q5=makeQuery(id+"F8.boolean.opBoolean","INTERSECT",EDGE,{"disambiguationData":[OD(0.0)],"derivedFrom":[makeQuery(id+"F5.opExtrude","SWEPT_FACE",FACE,{"disambiguationData":[OSD([sQuery(id+"F4.wireOp",EDGE,"E30")])]}),makeQuery(id+"F8.opExtrude","SWEPT_FACE",FACE,{"disambiguationData":[OSD([sQuery(id+"F7.wireOp",EDGE,"E67")])]})]});
            fillet(context, id + "F14", {"entities" : qUnion([Q0, Q1, Q2, Q3, Q4, Q5]), "radius" : 3 * mm, "tangentPropagation" : true, "allowEdgeOverflow" : false});
        }
        {
            var Q0;
            Q0=makeQuery(id+"F1.opExtrude","CAP_EDGE",EDGE,{"disambiguationData":[OSD([sQuery(id+"F0.wireOp",EDGE,"E1.bottom")])],"isStart":false});
            fillet(context, id + "F15", {"entities" : qUnion([Q0]), "radius" : 2 * mm, "tangentPropagation" : true, "allowEdgeOverflow" : false});
        }
        {
            var Q0;
            {var subQ0=sQuery(id+"F0.wireOp",EDGE,"E22.filletArc");var subQ1=sQuery(id+"F0.wireOp",EDGE,"E7");var subQ2=sQuery(id+"F0.wireOp",EDGE,"E6");var subQ3=sQuery(id+"F0.wireOp",EDGE,"E5");var subQ4=sQuery(id+"F0.wireOp",EDGE,"E4");var subQ5=sQuery(id+"F0.wireOp",EDGE,"E1.bottom");var subQ6=sQuery(id+"F0.wireOp",EDGE,"E21.filletArc");var subQ7=sQuery(id+"F0.wireOp",EDGE,"E1.top");var subQ8=sQuery(id+"F0.wireOp",EDGE,"E1.left");var subQ9=sQuery(id+"F0.wireOp",EDGE,"E1.right");var subQ10=sQuery(id+"F0.wireOp",EDGE,"E23.filletArc");var subQ11=sQuery(id+"F0.wireOp",EDGE,"E24.filletArc");Q0=makeQuery(id+"F2.boolean.opBoolean","SPLIT",FACE,{"disambiguationData":[TD([makeQuery(id+"F1.opExtrude","SWEPT_FACE",FACE,{"disambiguationData":[OSD([subQ5])]})])],"derivedFrom":makeQuery(id+"F1.opExtrude","CAP_FACE",FACE,{"disambiguationData":[OSD([subQ5,subQ7,subQ8,subQ9,subQ4,subQ3,subQ2,subQ1,subQ6,subQ0,subQ10,subQ11])],"isStart":true})});}
            var sketch = newSketch(context, id + "F16", { "sketchPlane" : qUnion([Q0])});
            skLineSegment(sketch, "E79", {"start": v(0, 90) * mm, "end": v(0, 120) * mm, "construction": true});
            skCircle(sketch, "E80", {"center": v(0, 120) * mm, "radius": 6 * mm});
            skLineSegment(sketch, "E81", {"start": v(-33, 90) * mm, "end": v(-15, 108) * mm});
            skLineSegment(sketch, "E82", {"start": v(-15, 108) * mm, "end": v(-15, 108) * mm});
            skLineSegment(sketch, "E83.MirrorCS", {"start": v(33, 90) * mm, "end": v(15, 108) * mm});
            skLineSegment(sketch, "E84.MirrorCS", {"start": v(15, 108) * mm, "end": v(15, 108) * mm});
            skLineSegment(sketch, "E85", {"start": v(-80, 0) * mm, "end": v(80, 0) * mm, "construction": true});
            skLineSegment(sketch, "E86", {"start": v(-15, 108) * mm, "end": v(-15, 120) * mm});
            skLineSegment(sketch, "E87.MirrorCS", {"start": v(15, 108) * mm, "end": v(15, 120) * mm});
            skArc(sketch, "E88", {"start": v(15, 120) * mm, "mid": v(0, 135) * mm, "end": v(-15, 120) * mm});
            skLineSegment(sketch, "E89.MirrorCS", {"start": v(33, -90) * mm, "end": v(15, -108) * mm});
            skLineSegment(sketch, "E90.MirrorCS", {"start": v(15, -108) * mm, "end": v(15, -120) * mm});
            skArc(sketch, "E91.MirrorCS", {"start": v(15, -120) * mm, "mid": v(0, -135) * mm, "end": v(-15, -120) * mm});
            skCircle(sketch, "E92.MirrorC", {"center": v(0, -120) * mm, "radius": 6 * mm});
            skLineSegment(sketch, "E93.MirrorCS", {"start": v(0, -90) * mm, "end": v(0, -120) * mm, "construction": true});
            skLineSegment(sketch, "E94.MirrorCS", {"start": v(-33, -90) * mm, "end": v(-15, -108) * mm});
            skLineSegment(sketch, "E95.MirrorCS", {"start": v(-15, -108) * mm, "end": v(-15, -120) * mm});
            skSolve(sketch);
        }
        {
            var Q0;
            Q0=makeQuery(id+"F16.imprint","IMPRINT",FACE,{"disambiguationData":[TD([[makeQuery(id+"F16.imprint","IMPRINT",EDGE,{"derivedFrom":sQuery(id+"F16.wireOp",EDGE,"E80")}),-1.0]])]});
            var Q1;
            Q1=makeQuery(id+"F16.imprint","IMPRINT",FACE,{"disambiguationData":[TD([[makeQuery(id+"F16.imprint","IMPRINT",EDGE,{"derivedFrom":makeQuery(id+"F1.opExtrude","CAP_EDGE",EDGE,{"disambiguationData":[OSD([sQuery(id+"F0.wireOp",EDGE,"E1.left")])],"isStart":true})}),-1.0]])]});
            var Q2;
            {var subQ0=sQuery(id+"F16.wireOp",EDGE,"43fcbfa9-bb9a-400d-ab4d-6c7ff70e0f6b0.MirrorCS");Q2=makeQuery(id+"F16.imprint","IMPRINT",FACE,{"disambiguationData":[TD([[makeQuery(id+"F16.imprint","IMPRINT",EDGE,{"derivedFrom":subQ0}),-1.0]])]});}
            var Q3;
            {var subQ0=sQuery(id+"F16.wireOp",EDGE,"E89.MirrorCS");Q3=makeQuery(id+"F16.imprint","IMPRINT",FACE,{"disambiguationData":[TD([[makeQuery(id+"F16.imprint","IMPRINT",EDGE,{"derivedFrom":subQ0}),-1.0]])]});}
            var Q4;
            Q4=makeQuery(id+"F2.opExtrude","CAP_FACE",FACE,{"disambiguationData":[OSD([sQuery(id+"F0.wireOp",EDGE,"E12"),sQuery(id+"F0.wireOp",EDGE,"E13"),sQuery(id+"F0.wireOp",EDGE,"E14"),sQuery(id+"F0.wireOp",EDGE,"E15"),sQuery(id+"F0.wireOp",EDGE,"E17.filletArc"),sQuery(id+"F0.wireOp",EDGE,"E18.filletArc"),sQuery(id+"F0.wireOp",EDGE,"E19.filletArc"),sQuery(id+"F0.wireOp",EDGE,"E20.filletArc"),sQuery(id+"F0.wireOp",EDGE,"E25.0"),sQuery(id+"F0.wireOp",EDGE,"E25.1"),sQuery(id+"F0.wireOp",EDGE,"E25.2"),sQuery(id+"F0.wireOp",EDGE,"E25.3"),sQuery(id+"F0.wireOp",EDGE,"E25.4"),sQuery(id+"F0.wireOp",EDGE,"E25.5"),sQuery(id+"F0.wireOp",EDGE,"E25.6"),sQuery(id+"F0.wireOp",EDGE,"E25.7")])],"isStart":false});
            extrude(context, id + "F17", {"entities" : qUnion([Q0, Q1, Q2, Q3]), "endBound" : BoundingType.UP_TO_SURFACE, "endBoundEntityFace" : qUnion([Q4]), "depth" : 25 * mm});
        }
    });
